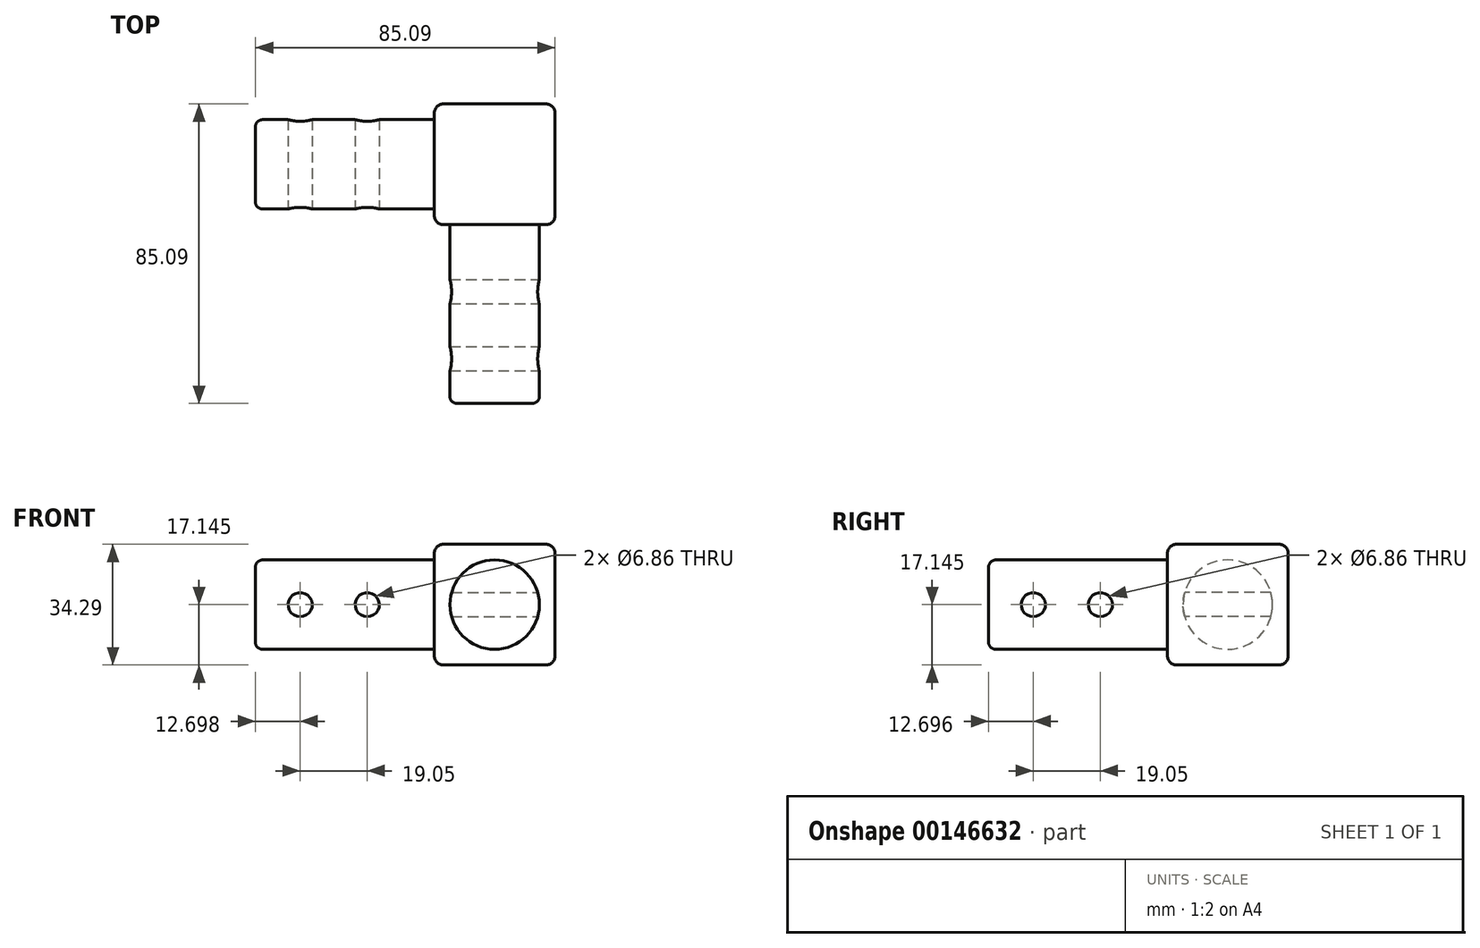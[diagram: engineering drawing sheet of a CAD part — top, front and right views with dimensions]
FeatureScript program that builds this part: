
annotation { "Feature Type Name" : "Feature", "Feature Type Description" : "" }
export const myFeature = defineFeature(function(context is Context, id is Id, definition is map)
    precondition{}
    {
        {
            var Q0;
            Q0=qCreatedBy(makeId("Top.planeOp"),FACE);
            var sketch = newSketch(context, id + "F0", { "sketchPlane" : qUnion([Q0])});
            skLineSegment(sketch, "E0.bottom", {"start": v(-13.47, 23.7) * mm, "end": v(20.82, 23.7) * mm});
            skLineSegment(sketch, "E0.top", {"start": v(-13.47, -10.58) * mm, "end": v(20.82, -10.58) * mm});
            skLineSegment(sketch, "E0.left", {"start": v(-13.47, 23.7) * mm, "end": v(-13.47, -10.58) * mm});
            skLineSegment(sketch, "E0.right", {"start": v(20.82, 23.7) * mm, "end": v(20.82, -10.58) * mm});
            skSolve(sketch);
        }
        {
            var Q0;
            Q0=qSketchRegion(id+"F0",true);
            extrude(context, id + "F1", {"entities" : qUnion([Q0]), "depth" : 34.3 * mm});
        }
        {
            var Q0;
            Q0=makeQuery(id+"F1.opExtrude","SWEPT_FACE",FACE,{"disambiguationData":[OSD([sQuery(id+"F0.wireOp",EDGE,"E0.left")])]});
            var sketch = newSketch(context, id + "F2", { "sketchPlane" : qUnion([Q0])});
            skLineSegment(sketch, "E1", {"start": v(-23.7, 17.15) * mm, "end": v(13.45, 17.15) * mm, "construction": true});
            skLineSegment(sketch, "E2", {"start": v(-6.56, 0) * mm, "end": v(-6.56, 34.3) * mm, "construction": true});
            skCircle(sketch, "E3", {"center": v(-6.56, 17.15) * mm, "radius": 12.7 * mm});
            skSolve(sketch);
        }
        {
            var Q0;
            Q0=qSketchRegion(id+"F2",true);
            extrude(context, id + "F3", {"entities" : qUnion([Q0]), "operationType" : NewBodyOperationType.ADD, "depth" : 50.8 * mm});
        }
        {
            var Q0;
            Q0=makeQuery(id+"F1.opExtrude","SWEPT_FACE",FACE,{"disambiguationData":[OSD([sQuery(id+"F0.wireOp",EDGE,"E0.top")])]});
            var sketch = newSketch(context, id + "F4", { "sketchPlane" : qUnion([Q0])});
            skLineSegment(sketch, "E4", {"start": v(-13.47, 17.15) * mm, "end": v(24.43, 17.15) * mm, "construction": true});
            skLineSegment(sketch, "E5", {"start": v(3.67, 0) * mm, "end": v(3.67, 34.3) * mm, "construction": true});
            skCircle(sketch, "E6", {"center": v(3.67, 17.15) * mm, "radius": 12.7 * mm});
            skSolve(sketch);
        }
        {
            var Q0;
            Q0=qSketchRegion(id+"F4",true);
            extrude(context, id + "F5", {"entities" : qUnion([Q0]), "operationType" : NewBodyOperationType.ADD, "depth" : 50.8 * mm});
        }
        {
            var Q0;
            Q0=qCreatedBy(makeId("Front.planeOp"),FACE);
            var sketch = newSketch(context, id + "F6", { "sketchPlane" : qUnion([Q0])});
            skCircle(sketch, "E7", {"center": v(3.67, 53.34) * mm, "radius": 3.43 * mm});
            skCircle(sketch, "E8", {"center": v(3.67, 72.4) * mm, "radius": 3.43 * mm});
            skSolve(sketch);
        }
        {
            var Q0;
            Q0=qSketchRegion(id+"F6",true);
            extrude(context, id + "F7", {"entities" : qUnion([Q0]), "operationType" : NewBodyOperationType.REMOVE, "endBound" : BoundingType.SYMMETRIC, "oppositeDirection" : true, "depth" : 50.8 * mm});
        }
        {
            var Q0;
            Q0=qCreatedBy(makeId("Right.planeOp"),FACE);
            var sketch = newSketch(context, id + "F8", { "sketchPlane" : qUnion([Q0])});
            skCircle(sketch, "E9", {"center": v(-29.63, 17.15) * mm, "radius": 3.43 * mm});
            skCircle(sketch, "E10", {"center": v(-48.68, 17.15) * mm, "radius": 3.43 * mm});
            skSolve(sketch);
        }
        {
            var Q0;
            Q0=qSketchRegion(id+"F8",true);
            extrude(context, id + "F9", {"entities" : qUnion([Q0]), "operationType" : NewBodyOperationType.REMOVE, "endBound" : BoundingType.SYMMETRIC, "oppositeDirection" : true, "depth" : 50.8 * mm});
        }
        {
            var Q0;
            Q0=qCreatedBy(makeId("Front.planeOp"),FACE);
            var sketch = newSketch(context, id + "F10", { "sketchPlane" : qUnion([Q0])});
            skCircle(sketch, "E11", {"center": v(-51.57, 17.15) * mm, "radius": 3.43 * mm});
            skCircle(sketch, "E12", {"center": v(-32.52, 17.15) * mm, "radius": 3.43 * mm});
            skSolve(sketch);
        }
        {
            var Q0;
            Q0=qSketchRegion(id+"F10",true);
            extrude(context, id + "F11", {"entities" : qUnion([Q0]), "operationType" : NewBodyOperationType.REMOVE, "endBound" : BoundingType.SYMMETRIC, "oppositeDirection" : true, "depth" : 50.8 * mm});
        }
        {
            var Q0;
            Q0=makeQuery(id+"Ff8LsmKBHV4Uzf6_1.opExtrude","CAP_EDGE",EDGE,{"disambiguationData":[OSD([sQuery(id+"FGSIiZxj4pOu3NG_1.wireOp",EDGE,"UelfSfaY-AMup-COUh-hXSA-o5mW5rKARTS6")])],"isStart":false});
            var Q1;
            Q1=makeQuery(id+"F5.opExtrude","CAP_EDGE",EDGE,{"disambiguationData":[OSD([sQuery(id+"F4.wireOp",EDGE,"E6")])],"isStart":false});
            var Q2;
            Q2=makeQuery(id+"F3.opExtrude","CAP_EDGE",EDGE,{"disambiguationData":[OSD([sQuery(id+"F2.wireOp",EDGE,"E3")])],"isStart":false});
            fillet(context, id + "F12", {"entities" : qUnion([Q0, Q1, Q2]), "radius" : 2.03 * mm, "tangentPropagation" : true, "allowEdgeOverflow" : false});
        }
        {
            var Q0;
            Q0=makeQuery(id+"F1.opExtrude","SWEPT_EDGE",EDGE,{"disambiguationData":[OSD([sQuery(id+"F0.wireOp",EDGE,"E0.bottom"),sQuery(id+"F0.wireOp",EDGE,"E0.right")])]});
            var Q1;
            Q1=makeQuery(id+"F1.opExtrude","CAP_EDGE",EDGE,{"disambiguationData":[OSD([sQuery(id+"F0.wireOp",EDGE,"E0.right")])],"isStart":false});
            var Q2;
            Q2=makeQuery(id+"F1.opExtrude","SWEPT_EDGE",EDGE,{"disambiguationData":[OSD([sQuery(id+"F0.wireOp",EDGE,"E0.top"),sQuery(id+"F0.wireOp",EDGE,"E0.right")])]});
            var Q3;
            Q3=makeQuery(id+"F1.opExtrude","CAP_EDGE",EDGE,{"disambiguationData":[OSD([sQuery(id+"F0.wireOp",EDGE,"E0.right")])],"isStart":true});
            var Q4;
            Q4=makeQuery(id+"F1.opExtrude","CAP_EDGE",EDGE,{"disambiguationData":[OSD([sQuery(id+"F0.wireOp",EDGE,"E0.bottom")])],"isStart":true});
            var Q5;
            Q5=makeQuery(id+"F1.opExtrude","CAP_EDGE",EDGE,{"disambiguationData":[OSD([sQuery(id+"F0.wireOp",EDGE,"E0.bottom")])],"isStart":false});
            var Q6;
            Q6=makeQuery(id+"F1.opExtrude","SWEPT_EDGE",EDGE,{"disambiguationData":[OSD([sQuery(id+"F0.wireOp",EDGE,"E0.bottom"),sQuery(id+"F0.wireOp",EDGE,"E0.left")])]});
            var Q7;
            Q7=makeQuery(id+"F1.opExtrude","CAP_EDGE",EDGE,{"disambiguationData":[OSD([sQuery(id+"F0.wireOp",EDGE,"E0.left")])],"isStart":true});
            var Q8;
            Q8=makeQuery(id+"F1.opExtrude","CAP_EDGE",EDGE,{"disambiguationData":[OSD([sQuery(id+"F0.wireOp",EDGE,"E0.top")])],"isStart":true});
            var Q9;
            Q9=makeQuery(id+"F1.opExtrude","CAP_EDGE",EDGE,{"disambiguationData":[OSD([sQuery(id+"F0.wireOp",EDGE,"E0.left")])],"isStart":false});
            var Q10;
            Q10=makeQuery(id+"F1.opExtrude","SWEPT_EDGE",EDGE,{"disambiguationData":[OSD([sQuery(id+"F0.wireOp",EDGE,"E0.top"),sQuery(id+"F0.wireOp",EDGE,"E0.left")])]});
            var Q11;
            Q11=makeQuery(id+"F1.opExtrude","CAP_EDGE",EDGE,{"disambiguationData":[OSD([sQuery(id+"F0.wireOp",EDGE,"E0.top")])],"isStart":false});
            fillet(context, id + "F13", {"entities" : qUnion([Q0, Q1, Q2, Q3, Q4, Q5, Q6, Q7, Q8, Q9, Q10, Q11]), "radius" : 2.54 * mm, "tangentPropagation" : true, "allowEdgeOverflow" : false});
        }
    });
